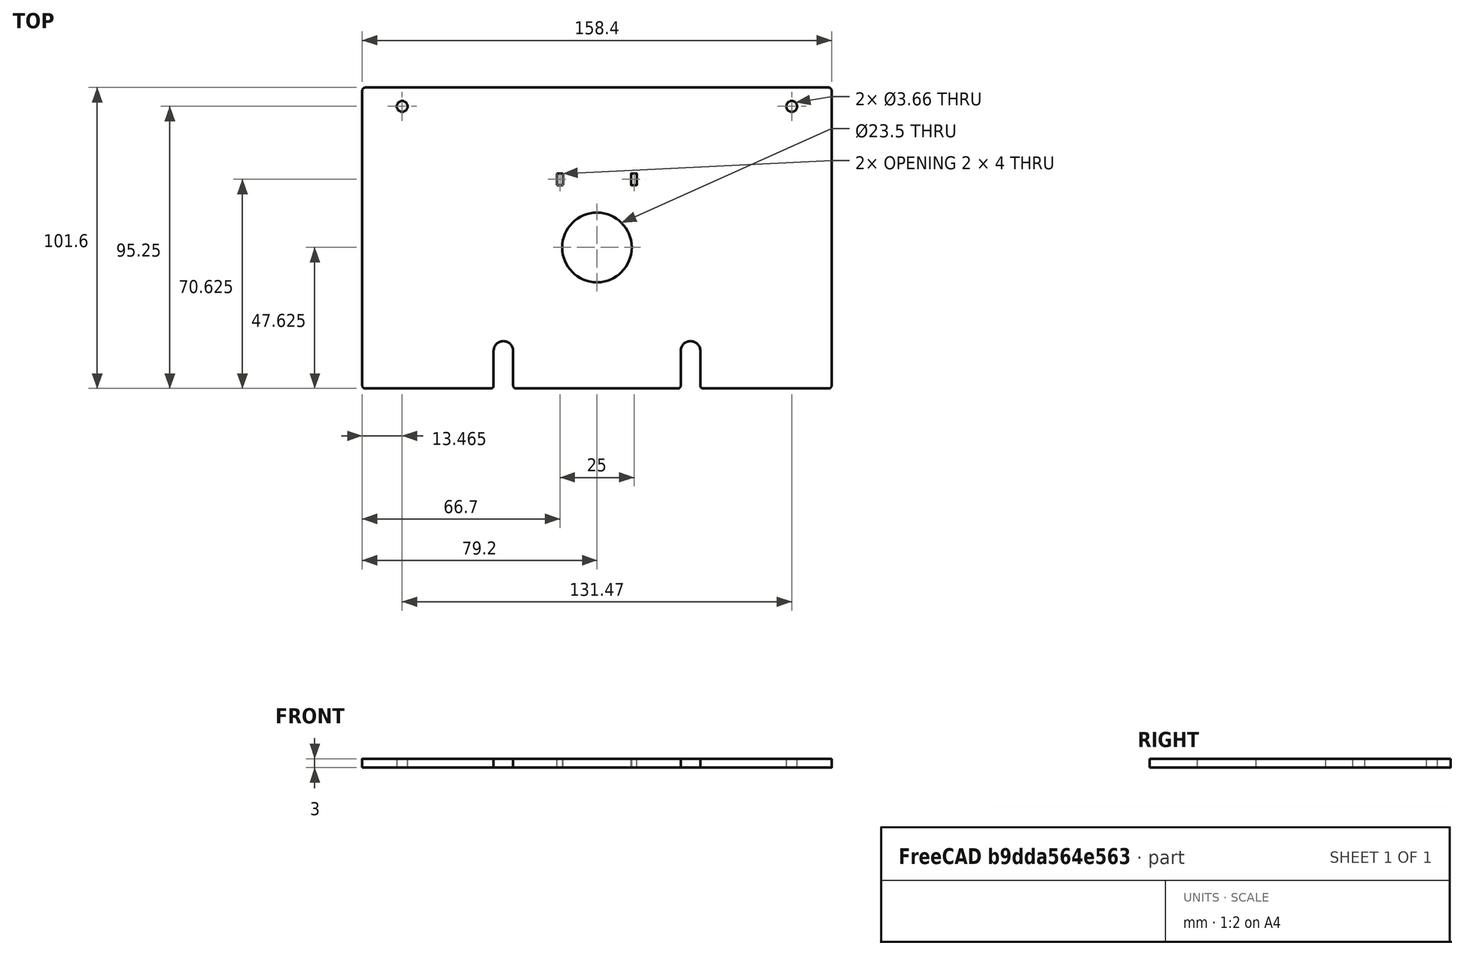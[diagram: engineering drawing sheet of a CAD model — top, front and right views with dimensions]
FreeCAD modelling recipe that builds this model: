
FCSTD DOCUMENT  (FreeCAD 0.21R33675 (Git))
Label: feeding_box_back
License: All rights reserved
LicenseURL: http://en.wikipedia.org/wiki/All_rights_reserved
objects: Sketcher::SketchObject×1, Spreadsheet::Sheet×1, PartDesign::Pad×1, PartDesign::Body×1
note: 4 computed .brp shape members not serialized (recipe doc carries the construction recipe); baked Part::Feature solids carry a one-line shape summary decoded from their .brp

FEATURE [Sketcher::SketchObject] Sketch
  FullyConstrained = true
  MapMode = 5
  Support = -> [XY_Plane]
  expr: Constraints[111] = Spreadsheet.ZipTieHoleFilletRadius
  expr: Constraints[112] = Spreadsheet.ZipTieHoleHeight
  expr: Constraints[113] = Spreadsheet.ZipTieHoleWidth
  expr: Constraints[114] = Spreadsheet.MountHoleDiameter
  expr: Constraints[120] = Spreadsheet.BracketHoleFromSide
  expr: Constraints[121] = Spreadsheet.UpperBracketHoleFromTop
  expr: Constraints[134] = Spreadsheet.BracketHoleFromSide
  expr: Constraints[135] = Spreadsheet.UpperBracketHoleFromTop
  expr: Constraints[143] = Spreadsheet.BracketHoleDiameter
  expr: Constraints[19] = Spreadsheet.FilletRadius
  expr: Constraints[21] = Spreadsheet.Height
  expr: Constraints[22] = Spreadsheet.Length
  expr: Constraints[30] = Spreadsheet.MountHoleSideMargin
  expr: Constraints[36] = Spreadsheet.MountHoleDistanceFromBottom
  expr: Constraints[39] = Spreadsheet.FeederHoleDiameter
  expr: Constraints[43] = Spreadsheet.FloorHeight
  expr: Constraints[55] = Spreadsheet.ZipTieMountHeight
  expr: Constraints[56] = Spreadsheet.ZipTieMountWidth
  expr: Constraints[82] = Spreadsheet.ZipTieHoleHeight
  expr: Constraints[84] = Spreadsheet.ZipTieHoleWidth
  expr: Constraints[85] = Spreadsheet.ZipTieHoleFilletRadius
  sketch-geometry (71):
    g0: ArcOfCircle CenterX=-78.2 CenterY=49.8 CenterZ=0 NormalX=0 NormalY=0 NormalZ=1 AngleXU=0 Radius=1 StartAngle=1.5708 EndAngle=3.14159
    g1: LineSegment StartX=-78.2 StartY=50.8 StartZ=0 EndX=78.2 EndY=50.8 EndZ=0
    g2: ArcOfCircle CenterX=78.2 CenterY=49.8 CenterZ=0 NormalX=0 NormalY=0 NormalZ=1 AngleXU=0 Radius=1 StartAngle=1.3192e-12 EndAngle=1.5708
    g3: LineSegment StartX=79.2 StartY=49.8 StartZ=0 EndX=79.2 EndY=-49.8 EndZ=0
    g4: ArcOfCircle CenterX=78.2 CenterY=-49.8 CenterZ=0 NormalX=0 NormalY=0 NormalZ=1 AngleXU=0 Radius=1 StartAngle=4.71239 EndAngle=6.28319
    g5: LineSegment StartX=78.2 StartY=-50.8 StartZ=0 EndX=-78.2 EndY=-50.8 EndZ=0
    g6: ArcOfCircle CenterX=-78.2 CenterY=-49.8 CenterZ=0 NormalX=0 NormalY=0 NormalZ=1 AngleXU=0 Radius=1 StartAngle=3.14159 EndAngle=4.71239
    g7: LineSegment StartX=-79.2 StartY=-49.8 StartZ=0 EndX=-79.2 EndY=49.8 EndZ=0
    g8: GeomPoint X=-79.2 Y=50.8 Z=0
    g9: GeomPoint X=79.2 Y=-50.8 Z=0
    g10: LineSegment StartX=-31.575 StartY=-38.1 StartZ=0 EndX=-79.2 EndY=-38.1 EndZ=0
    g11: LineSegment StartX=31.575 StartY=-38.1 StartZ=0 EndX=79.2 EndY=-38.1 EndZ=0
    g12: Circle CenterX=-31.575 CenterY=-38.1 CenterZ=0 NormalX=0 NormalY=0 NormalZ=1 AngleXU=0 Radius=3.302
    g13: Circle CenterX=31.575 CenterY=-38.1 CenterZ=0 NormalX=0 NormalY=0 NormalZ=1 AngleXU=0 Radius=3.302
    g14: LineSegment StartX=0 StartY=-38.1 StartZ=0 EndX=0 EndY=-50.8 EndZ=0
    g15: LineSegment StartX=-31.575 StartY=-38.1 StartZ=0 EndX=0 EndY=-38.1 EndZ=0
    g16: LineSegment StartX=0 StartY=-38.1 StartZ=0 EndX=31.575 EndY=-38.1 EndZ=0
    g17: Circle CenterX=-2.2e-15 CenterY=-3.175 CenterZ=0 NormalX=0 NormalY=0 NormalZ=1 AngleXU=0 Radius=11.75
    g18: LineSegment StartX=-79.2 StartY=-22.225 StartZ=0 EndX=79.2 EndY=-22.225 EndZ=0
    g19: LineSegment StartX=-2.2e-15 StartY=19.825 StartZ=0 EndX=12.5 EndY=19.825 EndZ=0
    g20: LineSegment StartX=-2.2e-15 StartY=19.825 StartZ=0 EndX=-12.5 EndY=19.825 EndZ=0
    g21: LineSegment StartX=-2.2e-15 StartY=19.825 StartZ=0 EndX=-2.2e-15 EndY=-3.175 EndZ=0
    g22: LineSegment StartX=-2.2e-15 StartY=-22.225 StartZ=0 EndX=-2.2e-15 EndY=-3.175 EndZ=0
    g23: GeomPoint X=-12.5 Y=19.825 Z=0
    g24: ArcOfCircle CenterX=-13.3 CenterY=21.625 CenterZ=0 NormalX=0 NormalY=0 NormalZ=1 AngleXU=0 Radius=0.2 StartAngle=1.5708 EndAngle=3.14159
    g25: LineSegment StartX=-13.3 StartY=21.825 StartZ=0 EndX=-11.7 EndY=21.825 EndZ=0
    g26: ArcOfCircle CenterX=-11.7 CenterY=21.625 CenterZ=0 NormalX=0 NormalY=0 NormalZ=1 AngleXU=0 Radius=0.2 StartAngle=0 EndAngle=1.5708
    g27: LineSegment StartX=-11.5 StartY=21.625 StartZ=0 EndX=-11.5 EndY=18.025 EndZ=0
    g28: ArcOfCircle CenterX=-11.7 CenterY=18.025 CenterZ=0 NormalX=0 NormalY=0 NormalZ=1 AngleXU=0 Radius=0.2 StartAngle=4.71239 EndAngle=6.28319
    g29: LineSegment StartX=-11.7 StartY=17.825 StartZ=0 EndX=-13.3 EndY=17.825 EndZ=0
    g30: ArcOfCircle CenterX=-13.3 CenterY=18.025 CenterZ=0 NormalX=0 NormalY=0 NormalZ=1 AngleXU=0 Radius=0.2 StartAngle=3.14159 EndAngle=4.71239
    g31: LineSegment StartX=-13.5 StartY=18.025 StartZ=0 EndX=-13.5 EndY=21.625 EndZ=0
    g32: GeomPoint X=-13.5 Y=21.825 Z=0
    g33: GeomPoint X=-11.5 Y=17.825 Z=0
    g34: LineSegment StartX=-13.5 StartY=21.825 StartZ=0 EndX=-12.5 EndY=19.825 EndZ=0
    g35: LineSegment StartX=-12.5 StartY=19.825 StartZ=0 EndX=-11.5 EndY=17.825 EndZ=0
    g36: ArcOfCircle CenterX=11.7 CenterY=21.625 CenterZ=0 NormalX=0 NormalY=0 NormalZ=1 AngleXU=0 Radius=0.2 StartAngle=1.5708 EndAngle=3.14159
    g37: LineSegment StartX=11.7 StartY=21.825 StartZ=0 EndX=13.3 EndY=21.825 EndZ=0
    g38: ArcOfCircle CenterX=13.3 CenterY=21.625 CenterZ=0 NormalX=0 NormalY=0 NormalZ=1 AngleXU=0 Radius=0.2 StartAngle=5e-15 EndAngle=1.5708
    g39: LineSegment StartX=13.5 StartY=21.625 StartZ=0 EndX=13.5 EndY=18.025 EndZ=0
    g40: ArcOfCircle CenterX=13.3 CenterY=18.025 CenterZ=0 NormalX=0 NormalY=0 NormalZ=1 AngleXU=0 Radius=0.2 StartAngle=4.71239 EndAngle=6.28319
    g41: LineSegment StartX=13.3 StartY=17.825 StartZ=0 EndX=11.7 EndY=17.825 EndZ=0
    g42: ArcOfCircle CenterX=11.7 CenterY=18.025 CenterZ=0 NormalX=0 NormalY=0 NormalZ=1 AngleXU=0 Radius=0.2 StartAngle=3.14159 EndAngle=4.71239
    g43: LineSegment StartX=11.5 StartY=18.025 StartZ=0 EndX=11.5 EndY=21.625 EndZ=0
    g44: GeomPoint X=11.5 Y=21.825 Z=0
    g45: GeomPoint X=13.5 Y=17.825 Z=0
    g46: LineSegment StartX=11.5 StartY=21.825 StartZ=0 EndX=12.5 EndY=19.825 EndZ=0
    g47: LineSegment StartX=12.5 StartY=19.825 StartZ=0 EndX=13.5 EndY=17.825 EndZ=0
    g48: LineSegment StartX=-65.7352 StartY=50.8 StartZ=0 EndX=-65.7352 EndY=44.45 EndZ=0
    g49: LineSegment StartX=-65.7352 StartY=44.45 StartZ=0 EndX=-65.7352 EndY=8.74e-13 EndZ=0
    g50: LineSegment StartX=-65.7352 StartY=8.747e-13 StartZ=0 EndX=-79.2 EndY=8.747e-13 EndZ=0
    g51: LineSegment StartX=65.7352 StartY=50.8 StartZ=0 EndX=65.7352 EndY=44.45 EndZ=0
    g52: LineSegment StartX=65.7352 StartY=44.45 StartZ=0 EndX=65.7352 EndY=6.324e-13 EndZ=0
    g53: LineSegment StartX=65.7352 StartY=6.317e-13 StartZ=0 EndX=79.2 EndY=6.317e-13 EndZ=0
    g54: Circle CenterX=-65.7352 CenterY=44.45 CenterZ=0 NormalX=0 NormalY=0 NormalZ=1 AngleXU=0 Radius=1.8288
    g55: Circle CenterX=-65.7352 CenterY=8.747e-13 CenterZ=0 NormalX=0 NormalY=0 NormalZ=1 AngleXU=0 Radius=1.8288
    g56: Circle CenterX=65.7352 CenterY=6.317e-13 CenterZ=0 NormalX=0 NormalY=0 NormalZ=1 AngleXU=0 Radius=1.8288
    g57: Circle CenterX=65.7352 CenterY=44.45 CenterZ=0 NormalX=0 NormalY=0 NormalZ=1 AngleXU=0 Radius=1.8288
    g58: ArcOfCircle CenterX=-31.575 CenterY=-38.1 CenterZ=0 NormalX=0 NormalY=0 NormalZ=1 AngleXU=0 Radius=3.302 StartAngle=5e-16 EndAngle=3.14159
    g59: LineSegment StartX=-34.877 StartY=-38.1 StartZ=0 EndX=-34.877 EndY=-49.8 EndZ=0
    g60: LineSegment StartX=-28.273 StartY=-38.1 StartZ=0 EndX=-28.273 EndY=-49.8 EndZ=0
    g61: ArcOfCircle CenterX=-35.877 CenterY=-49.8 CenterZ=0 NormalX=0 NormalY=0 NormalZ=1 AngleXU=0 Radius=1 StartAngle=4.71239 EndAngle=6.28319
    g62: ArcOfCircle CenterX=-27.273 CenterY=-49.8 CenterZ=0 NormalX=0 NormalY=0 NormalZ=1 AngleXU=0 Radius=1 StartAngle=3.14159 EndAngle=4.71239
    g63: ArcOfCircle CenterX=31.575 CenterY=-38.1 CenterZ=0 NormalX=0 NormalY=0 NormalZ=1 AngleXU=0 Radius=3.302 StartAngle=2e-15 EndAngle=3.14159
    g64: LineSegment StartX=28.273 StartY=-38.1 StartZ=0 EndX=28.273 EndY=-49.8 EndZ=0
    g65: LineSegment StartX=34.877 StartY=-38.1 StartZ=0 EndX=34.877 EndY=-49.8 EndZ=0
    g66: ArcOfCircle CenterX=27.273 CenterY=-49.8 CenterZ=0 NormalX=0 NormalY=0 NormalZ=1 AngleXU=0 Radius=1 StartAngle=4.71239 EndAngle=6.28319
    g67: ArcOfCircle CenterX=35.877 CenterY=-49.8 CenterZ=0 NormalX=0 NormalY=0 NormalZ=1 AngleXU=0 Radius=1 StartAngle=3.14159 EndAngle=4.71239
    g68: LineSegment StartX=-78.2 StartY=-50.8 StartZ=0 EndX=-35.877 EndY=-50.8 EndZ=0
    g69: LineSegment StartX=-27.273 StartY=-50.8 StartZ=0 EndX=27.273 EndY=-50.8 EndZ=0
    g70: LineSegment StartX=35.877 StartY=-50.8 StartZ=0 EndX=78.2 EndY=-50.8 EndZ=0
  constraints (180):
    c: Tangent(g0,g1) = 1.5708
    c: Tangent(g1,g2) = 1.5708
    c: Tangent(g2,g3) = 1.5708
    c: Tangent(g3,g4) = 1.5708
    c: Tangent(g4,g5) = 1.5708
    c: Tangent(g5,g6) = 1.5708
    c: Tangent(g6,g7) = 1.5708
    c: Tangent(g7,g0) = 1.5708
    c: Horizontal(g1)
    c: Horizontal(g5)
    c: Vertical(g3)
    c: Vertical(g7)
    c: Equal(g0,g2)
    c: Equal(g2,g4)
    c: Equal(g4,g6)
    c: PointOnObject(g8,g1)
    c: PointOnObject(g8,g7)
    c: PointOnObject(g9,g3)
    c: PointOnObject(g9,g5)
    c: Radius(g2) = 1
    c: Symmetric(g8,g9,g-1)
    c: DistanceY(g4,g1) = 101.6
    c: DistanceX(g0,g2) = 158.4
    c: PointOnObject(g14,g5)
    c: PointOnObject(g14,g-2)
    c: PointOnObject(g10,g7)
    c: Horizontal(g10)
    c: PointOnObject(g11,g3)
    c: Horizontal(g11)
    c: Equal(g11,g10)
    c: DistanceX(g10,g10) = 47.625
    c: Vertical(g14)
    c: Coincident(g15,g12)
    c: Horizontal(g15)
    c: Coincident(g16,g13)
    c: Horizontal(g16)
    c: DistanceY(g14,g14) = 12.7
    c: Coincident(g10,g12)
    c: Coincident(g13,g11)
    c: Diameter(g17) = 23.5
    c: PointOnObject(g18,g7)
    c: PointOnObject(g18,g3)
    c: Horizontal(g18)
    c: DistanceY(g9,g18) = 28.575
    c: Horizontal(g19)
    c: Horizontal(g20)
    c: Coincident(g20,g19)
    c: Coincident(g21,g19)
    c: Vertical(g21)
    c: Coincident(g21,g17)
    c: Equal(g20,g19)
    c: Coincident(g22,g17)
    c: Vertical(g22)
    c: Symmetric(g18,g18,g22)
    c: DistanceY(g22,g17) = 19.05
    c: DistanceY(g21,g21) = 23
    c: DistanceX(g20,g19) = 25
    c: Coincident(g23,g20)
    c: Tangent(g24,g25) = 1.5708
    c: Tangent(g25,g26) = 1.5708
    c: Tangent(g26,g27) = 1.5708
    c: Tangent(g27,g28) = 1.5708
    c: Tangent(g28,g29) = 1.5708
    c: Tangent(g29,g30) = 1.5708
    c: Tangent(g30,g31) = 1.5708
    c: Tangent(g31,g24) = 1.5708
    c: Horizontal(g25)
    c: Horizontal(g29)
    c: Vertical(g27)
    c: Vertical(g31)
    c: Equal(g24,g26)
    c: Equal(g26,g28)
    c: Equal(g28,g30)
    c: PointOnObject(g32,g25)
    c: PointOnObject(g32,g31)
    c: PointOnObject(g33,g27)
    c: PointOnObject(g33,g29)
    c: Coincident(g34,g32)
    c: Coincident(g34,g35)
    c: Coincident(g35,g33)
    c: Equal(g34,g35)
    c: Parallel(g34,g35)
    c: DistanceY(g33,g32) = 4
    c: Coincident(g34,g20)
    c: DistanceX(g24,g26) = 2
    c: Radius(g26) = 0.2
    c: Tangent(g36,g37) = 1.5708
    c: Tangent(g37,g38) = 1.5708
    c: Tangent(g38,g39) = 1.5708
    c: Tangent(g39,g40) = 1.5708
    c: Tangent(g40,g41) = 1.5708
    c: Tangent(g41,g42) = 1.5708
    c: Tangent(g42,g43) = 1.5708
    c: Tangent(g43,g36) = 1.5708
    c: Horizontal(g37)
    c: Horizontal(g41)
    c: Vertical(g39)
    c: Vertical(g43)
    c: Equal(g36,g38)
    c: Equal(g38,g40)
    c: Equal(g40,g42)
    c: PointOnObject(g44,g37)
    c: PointOnObject(g44,g43)
    c: PointOnObject(g45,g39)
    c: PointOnObject(g45,g41)
    c: Coincident(g46,g44)
    c: Coincident(g46,g47)
    c: Coincident(g47,g45)
    c: Parallel(g46,g47)
    c: Equal(g46,g47)
    c: Coincident(g46,g19)
    c: Radius(g38) = 0.2
    c: DistanceY(g40,g37) = 4
    c: DistanceX(g42,g39) = 2
    c: Diameter(g13) = 6.604
    c: Coincident(g16,g14)
    c: Coincident(g15,g14)
    c: Equal(g12,g13)
    c: PointOnObject(g48,g1)
    c: Vertical(g48)
    c: DistanceX(g8,g48) = 13.4648
    c: DistanceY(g48,g48) = 6.35
    c: Coincident(g49,g48)
    c: Vertical(g49)
    c: Coincident(g50,g49)
    c: Horizontal(g50)
    c: Symmetric(g0,g6,g50)
    c: PointOnObject(g51,g1)
    c: Vertical(g51)
    c: Coincident(g52,g51)
    c: Vertical(g52)
    c: Coincident(g53,g52)
    c: Horizontal(g53)
    c: Symmetric(g2,g3,g53)
    c: DistanceX(g51,g2) = 13.4648
    c: DistanceY(g51,g51) = 6.35
    c: Coincident(g54,g48)
    c: Coincident(g55,g49)
    c: Coincident(g56,g52)
    c: Coincident(g57,g51)
    c: Equal(g54,g57)
    c: Equal(g57,g56)
    c: Equal(g56,g55)
    c: Diameter(g54) = 3.6576
    c: Coincident(g58,g10)
    c: PointOnObject(g58,g10)
    c: PointOnObject(g58,g15)
    c: PointOnObject(g58,g12)
    c: Coincident(g59,g58)
    c: Vertical(g59)
    c: Coincident(g60,g58)
    c: Vertical(g60)
    c: Tangent(g61,g59) = 1.5708
    c: Tangent(g62,g5) = 1.5708
    c: Tangent(g62,g60) = -1.5708
    c: Tangent(g61,g5) = 1.5708
    c: Equal(g61,g62)
    c: Equal(g6,g61)
    c: Coincident(g63,g11)
    c: PointOnObject(g63,g16)
    c: PointOnObject(g63,g11)
    c: PointOnObject(g63,g13)
    c: Coincident(g64,g63)
    c: Vertical(g64)
    c: Coincident(g65,g63)
    c: Vertical(g65)
    c: Equal(g64,g65)
    c: Tangent(g66,g64) = 1.5708
    c: Tangent(g66,g5) = 1.5708
    c: Tangent(g67,g65) = -1.5708
    c: Tangent(g67,g5) = 1.5708
    c: Equal(g67,g4)
    c: Coincident(g68,g6)
    c: Coincident(g68,g61)
    c: Horizontal(g68)
    c: Tangent(g68,g61)
    c: Coincident(g69,g62)
    c: Coincident(g69,g66)
    c: Coincident(g70,g67)
    c: Coincident(g70,g4)
FEATURE [Spreadsheet::Sheet] Spreadsheet
  cells = A2='Parameters; A3='Height; B3(Height)==4 in; A4='Length; B4(Length)==158.4 mm; A5='Thickness; B5(Thickness)==3 mm; A6='FilletRadius; B6(FilletRadius)==1 mm; A7='MountHoleDiameter; B7(MountHoleDiameter)==0.26 in; A8='MountHoleDistanceFromBottom; B8(MountHoleDistanceFromBottom)==0.5 in; A9='MountHoleSideMargin; B9(MountHoleSideMargin)==1.875 in; A10='BeamHeight; B10(BeamHeight)==1 in; A11='FloorHeight; B11(FloorHeight)==BeamHeight + 0.125 in; A12='FeederHoleDiameter; B12(FeederHoleDiameter)==23.5 mm; A13='FeederHoleHeight; B13(FeederHoleHeight)==0.75 in; A14='ZipTieMountHeight; B14(ZipTieMountHeight)==23 mm; A15='ZipTieMountWidth; B15(ZipTieMountWidth)==25 mm; A16='ZipTieHoleWidth; B16(ZipTieHoleWidth)==2 mm; A17='ZipTieHoleHeight; B17(ZipTieHoleHeight)==4 mm; A18='ZipTieHoleFilletRadius; B18(ZipTieHoleFilletRadius)==0.2 mm; A20='BracketWidth; B20(BracketWidth)==0.5 in; A21='BracketHoleDiameter; B21(BracketHoleDiameter)==0.144 in; A22='BracketHoleOffset; B22(BracketHoleOffset)==0.412 in; A23='UpperBracketHoleFromTop; B23(UpperBracketHoleFromTop)==0.5 * BracketWidth; A24='BracketHoleFromSide; B24(BracketHoleFromSide)==BracketHoleOffset + Thickness
FEATURE [PartDesign::Pad] Pad
  Direction = (0,0,1)
  Length = 3
  Length2 = 10
  Profile = -> Sketch
  ReferenceAxis = -> Sketch [N_Axis]
  Type = 0
  expr: Length = Spreadsheet.Thickness
FEATURE [PartDesign::Body] Body
  Group = -> [Sketch,Pad]
  Origin = -> Origin
  Tip = -> Pad
